# Revit family: E_Cable Tray Support_MEPcontent_OBO Bettermann_Bracket AWG FT
name_source: partatom
category: Cable Tray Fittings
revit_build: Autodesk Revit MEP 2015 (Build: 20140606_1530(x64)
units: mm (PartAtom-declared; Revit-internal decimal feet)

## types (2) — shared parameters
Article Description = Wall Bracket
Depth = 40 mm  [stored 0.131234 ft]
Description = Wall Bracket
EMCS Version = 2.0
ETIM Article Class = EC000022
Family Version = 10.14
Gray = Color RGB 189-187-185
IFCExportAs = IfcCableCarrierFittingType
IFCExportType = NOTDEFINED
MEPcontent Class = CABLE_TRAY_SUPPORT
Manufacturer = OBO BETTERMANN
Manufacturer URL = http://catalog4.obo-bettermann.com
Product Line = OBO BETTERMANN CableTrays
Revit Version = 2015
URL = www.stabiplan.com

## per-type parameters (varying)
| type | Front Height | GTIN | Height | Height 1 | Manufacturer Art. No. | Width | Width 1 |
| AWG 15 16 FT | 13.75 mm  [stored 0.0451115 ft] | 4012196079155 | 55 mm | 55 mm  [stored 0.180446 ft] | 6420607 | 160 mm | 160 mm  [stored 0.524934 ft] |
| AWG 15 21 FT | 15 mm  [stored 0.0492126 ft] | 4012196662531 | 60 mm | 60 mm  [stored 0.19685 ft] | 6420608 | 210 mm | 210 mm  [stored 0.688976 ft] |

note: column(s) folded — value = type name in every type: Article Type, Model

note: [stored X ft] marks values corroborated as IEEE doubles in the binary element streams (Revit-internal decimal feet)

## geometry (parser evidence)
native form markers: Blend x4, Sweep x3
no freeform markers — native parametric forms only
